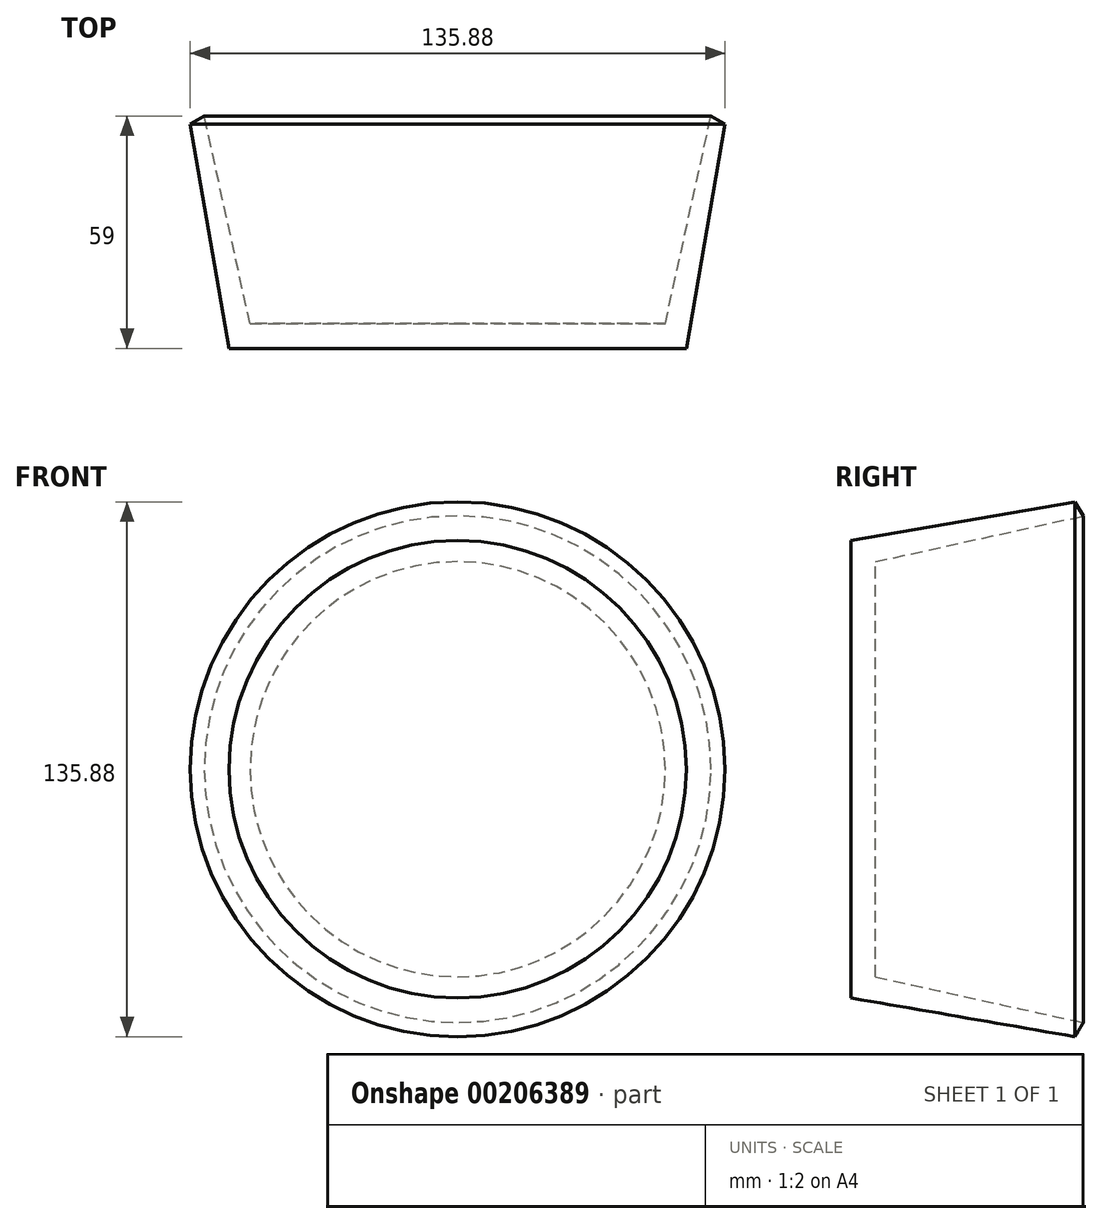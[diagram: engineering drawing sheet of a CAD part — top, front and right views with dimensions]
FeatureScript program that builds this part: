
annotation { "Feature Type Name" : "Feature", "Feature Type Description" : "" }
export const myFeature = defineFeature(function(context is Context, id is Id, definition is map)
    precondition{}
    {
        {
            var Q0;
            Q0=qCreatedBy(makeId("Top.planeOp"),FACE);
            var sketch = newSketch(context, id + "F0", { "sketchPlane" : qUnion([Q0])});
            skLineSegment(sketch, "E0", {"start": v(-63.47, 37.4) * mm, "end": v(-53.64, -19.52) * mm});
            skLineSegment(sketch, "E1", {"start": v(-53.64, -19.52) * mm, "end": v(4.47, -19.52) * mm});
            skLineSegment(sketch, "E2", {"start": v(4.47, -19.52) * mm, "end": v(4.47, -13.26) * mm});
            skLineSegment(sketch, "E3", {"start": v(4.47, -13.26) * mm, "end": v(-48.27, -13.26) * mm});
            skLineSegment(sketch, "E4", {"start": v(-48.27, -13.26) * mm, "end": v(-59.9, 39.48) * mm});
            skLineSegment(sketch, "E5", {"start": v(-59.9, 39.48) * mm, "end": v(-63.47, 37.4) * mm});
            skSolve(sketch);
        }
        {
            var Q0;
            Q0=makeQuery(id+"F0.imprint","IMPRINT",FACE,{"disambiguationData":[TD([[makeQuery(id+"F0.imprint","IMPRINT",EDGE,{"derivedFrom":sQuery(id+"F0.wireOp",EDGE,"E0")}),1.0]])]});
            var Q1;
            Q1=sQuery(id+"F0.wireOp",EDGE,"E2");
            revolve(context, id + "F1", {"entities" : qUnion([Q0]), "axis" : qUnion([Q1]), "revolveType" : RevolveType.FULL});
        }
    });
